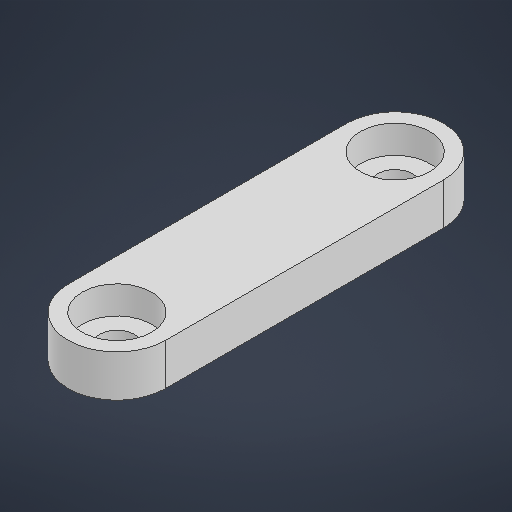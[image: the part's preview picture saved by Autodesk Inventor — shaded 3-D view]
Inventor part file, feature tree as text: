
AUTODESK INVENTOR PART (.ipt)
format: ipt  version: 2025.1 (Build 291241000, 241)  size: 436,736 bytes
history: native  units: mm
features: extrude x2, sketch x1
ambient origin geometry x8: Origin, YZ Plane, XZ Plane, XY Plane, X Axis, Y Axis, Z Axis, Center Point
bodies: Solid1 (feature_tree)
feature tree (3):
  sketch  "Sketch1"  dims[d0=7.0mm d1=2.5mm d2=20.0mm d3=3.0mm d4=0.0mm d5=5.0mm d6=5.0mm d7=1.0mm d8=0.0mm]
  extrude  "Extrusion1"  Depth=2.5mm
  extrude  "Extrusion2"  Depth=20.0mm
